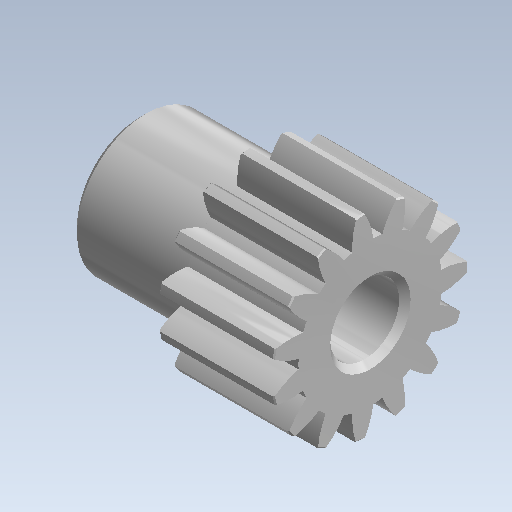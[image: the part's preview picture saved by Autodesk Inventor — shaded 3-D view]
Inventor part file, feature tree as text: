
AUTODESK INVENTOR PART (.ipt)
format: ipt  version: 2020.3 (Build 243373000, 373)  size: 272,384 bytes
history: native  units: mm (DEFAULTED — no unit token found)
features: sketch x2, revolve x1, extrude x1
ambient origin geometry x8: Origin, YZ Plane, XZ Plane, XY Plane, X Axis, Y Axis, Z Axis, Center Point
bodies: Solid1 (feature_tree)
feature tree (4):
  revolve  "Revolution1"  [1 undecoded]
  extrude  "Extrusion1"  [1 undecoded]
  sketch  "Sketch_8"  dims[d0=360.0deg d1=10.0mm d2=0.0mm]
  sketch  "Sketch_11"
note: 2 required parameter values undecoded (feature->parameter linkage not recoverable at this tier; creation-order binding heuristic only, values carry confidence <= 0.55)